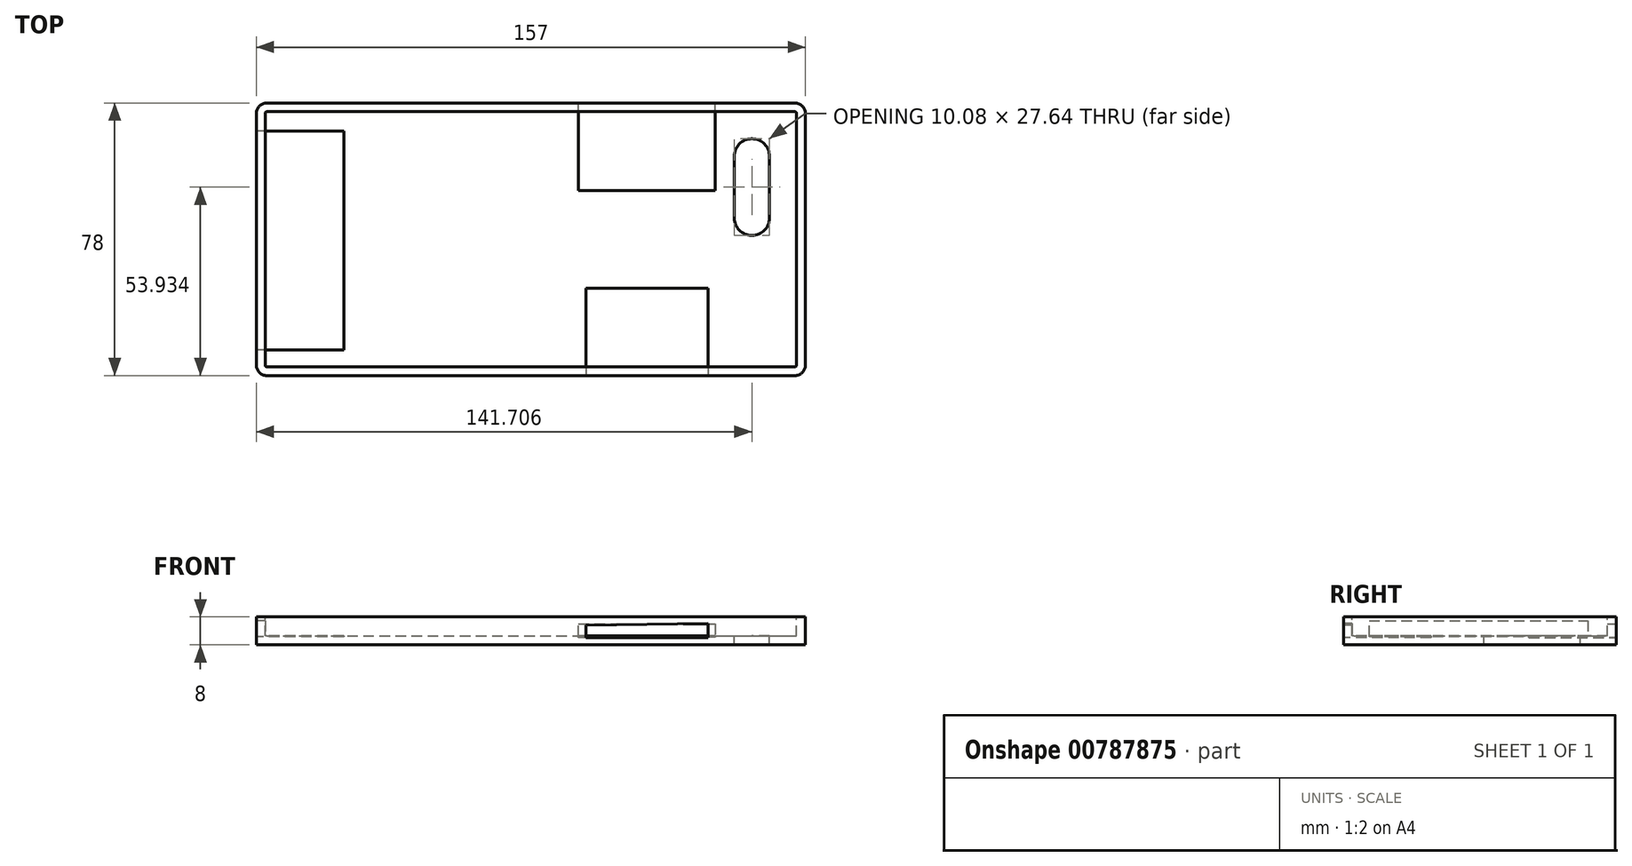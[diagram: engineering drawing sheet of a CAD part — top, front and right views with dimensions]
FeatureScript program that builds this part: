
annotation { "Feature Type Name" : "Feature", "Feature Type Description" : "" }
export const myFeature = defineFeature(function(context is Context, id is Id, definition is map)
    precondition{}
    {
        {
            var Q0;
            Q0=qCreatedBy(makeId("Top.planeOp"),FACE);
            var sketch = newSketch(context, id + "F0", { "sketchPlane" : qUnion([Q0])});
            skLineSegment(sketch, "E0.bottom", {"start": v(0, 0) * mm, "end": v(157, 0) * mm});
            skLineSegment(sketch, "E0.top", {"start": v(0, 78) * mm, "end": v(157, 78) * mm});
            skLineSegment(sketch, "E0.left", {"start": v(0, 0) * mm, "end": v(0, 78) * mm});
            skLineSegment(sketch, "E0.right", {"start": v(157, 0) * mm, "end": v(157, 78) * mm});
            skSolve(sketch);
        }
        {
            var Q0;
            Q0=makeQuery(id+"F0.imprint","IMPRINT",FACE,{"disambiguationData":[TD([[makeQuery(id+"F0.imprint","IMPRINT",EDGE,{"derivedFrom":sQuery(id+"F0.wireOp",EDGE,"E0.bottom")}),1.0]])]});
            extrude(context, id + "F1", {"entities" : qUnion([Q0]), "depth" : 8 * mm, "offsetDistance" : 25 * mm});
        }
        {
            var Q0;
            Q0=makeQuery(id+"F1.opExtrude","SWEPT_EDGE",EDGE,{"disambiguationData":[OSD([sQuery(id+"F0.wireOp",EDGE,"E0.bottom"),sQuery(id+"F0.wireOp",EDGE,"E0.right")])]});
            var Q1;
            Q1=makeQuery(id+"F1.opExtrude","SWEPT_EDGE",EDGE,{"disambiguationData":[OSD([sQuery(id+"F0.wireOp",EDGE,"E0.top"),sQuery(id+"F0.wireOp",EDGE,"E0.right")])]});
            var Q2;
            Q2=makeQuery(id+"F1.opExtrude","SWEPT_EDGE",EDGE,{"disambiguationData":[OSD([sQuery(id+"F0.wireOp",EDGE,"E0.top"),sQuery(id+"F0.wireOp",EDGE,"E0.left")])]});
            var Q3;
            Q3=makeQuery(id+"F1.opExtrude","SWEPT_EDGE",EDGE,{"disambiguationData":[OSD([sQuery(id+"F0.wireOp",EDGE,"E0.bottom"),sQuery(id+"F0.wireOp",EDGE,"E0.left")])]});
            fillet(context, id + "F2", {"entities" : qUnion([Q0, Q1, Q2, Q3]), "radius" : 3 * mm, "tangentPropagation" : true, "allowEdgeOverflow" : false});
        }
        {
            var Q0;
            Q0=makeQuery(id+"F1.opExtrude","CAP_FACE",FACE,{"disambiguationData":[OSD([sQuery(id+"F0.wireOp",EDGE,"E0.bottom"),sQuery(id+"F0.wireOp",EDGE,"E0.top"),sQuery(id+"F0.wireOp",EDGE,"E0.left"),sQuery(id+"F0.wireOp",EDGE,"E0.right")])],"isStart":false});
            shell(context, id + "F3", {"entities" : qUnion([Q0]), "thickness" : 2.5 * mm});
        }
        {
            var Q0;
            Q0=makeQuery(id+"F3.opShell","OFFSET_FACE",FACE,{"disambiguationData":[OSD([sQuery(id+"F0.wireOp",EDGE,"E0.bottom"),sQuery(id+"F0.wireOp",EDGE,"E0.top"),sQuery(id+"F0.wireOp",EDGE,"E0.left"),sQuery(id+"F0.wireOp",EDGE,"E0.right")])]});
            var sketch = newSketch(context, id + "F4", { "sketchPlane" : qUnion([Q0])});
            skLineSegment(sketch, "E1.bottom", {"start": v(141.74, 67.75) * mm, "end": v(141.67, 67.75) * mm});
            skLineSegment(sketch, "E1.top", {"start": v(141.74, 40.12) * mm, "end": v(141.67, 40.12) * mm});
            skLineSegment(sketch, "E1.left", {"start": v(146.74, 62.75) * mm, "end": v(146.74, 45.12) * mm});
            skLineSegment(sketch, "E1.right", {"start": v(136.67, 62.75) * mm, "end": v(136.67, 45.12) * mm});
            skPoint(sketch, "E2.visualSharp", {"position": v(146.74, 67.75) * mm});
            skArc(sketch, "E2.filletArc", {"start": v(146.74, 62.75) * mm, "mid": v(145.28, 66.29) * mm, "end": v(141.74, 67.75) * mm});
            skPoint(sketch, "E3.visualSharp", {"position": v(136.67, 67.75) * mm});
            skArc(sketch, "E3.filletArc", {"start": v(141.67, 67.75) * mm, "mid": v(138.13, 66.29) * mm, "end": v(136.67, 62.75) * mm});
            skPoint(sketch, "E4.visualSharp", {"position": v(136.67, 40.12) * mm});
            skArc(sketch, "E4.filletArc", {"start": v(136.67, 45.12) * mm, "mid": v(138.13, 41.58) * mm, "end": v(141.67, 40.12) * mm});
            skPoint(sketch, "E5.visualSharp", {"position": v(146.74, 40.12) * mm});
            skArc(sketch, "E5.filletArc", {"start": v(141.74, 40.12) * mm, "mid": v(145.28, 41.58) * mm, "end": v(146.74, 45.12) * mm});
            skSolve(sketch);
        }
        {
            var Q0;
            Q0=makeQuery(id+"F4.imprint","IMPRINT",FACE,{"disambiguationData":[TD([[makeQuery(id+"F4.imprint","IMPRINT",EDGE,{"derivedFrom":sQuery(id+"F4.wireOp",EDGE,"E1.bottom")}),1.0]])]});
            extrude(context, id + "F5", {"entities" : qUnion([Q0]), "operationType" : NewBodyOperationType.REMOVE, "oppositeDirection" : true, "depth" : 25 * mm, "offsetDistance" : 25 * mm});
        }
        {
            var Q0;
            Q0=makeQuery(id+"F1.opExtrude","SWEPT_FACE",FACE,{"disambiguationData":[OSD([sQuery(id+"F0.wireOp",EDGE,"E0.left")])]});
            var sketch = newSketch(context, id + "F6", { "sketchPlane" : qUnion([Q0])});
            skSolve(sketch);
        }
        {
            var Q0;
            {var subQ0=sQuery(id+"F0.wireOp",EDGE,"E0.left");Q0=makeQuery(id+"F6.imprint","IMPRINT",FACE,{"disambiguationData":[TD([[makeQuery(id+"F6.imprint","IMPRINT",EDGE,{"derivedFrom":makeQuery(id+"F1.opExtrude","CAP_EDGE",EDGE,{"disambiguationData":[OSD([subQ0])],"isStart":true})}),-1.0]])]});}
            var sketch = newSketch(context, id + "F7", { "sketchPlane" : qUnion([Q0])});
            skLineSegment(sketch, "E6", {"start": v(-69.9, 6.86) * mm, "end": v(-69.9, 2.36) * mm});
            skLineSegment(sketch, "E7", {"start": v(-69.9, 2.36) * mm, "end": v(-7.36, 2.36) * mm});
            skLineSegment(sketch, "E8", {"start": v(-7.36, 2.36) * mm, "end": v(-7.36, 6.86) * mm});
            skLineSegment(sketch, "E9", {"start": v(-7.36, 6.86) * mm, "end": v(-69.9, 6.86) * mm});
            skSolve(sketch);
        }
        {
            var Q0;
            Q0 = qSketchRegion(id + "F7", true);
            extrude(context, id + "F8", {"entities" : qUnion([Q0]), "operationType" : NewBodyOperationType.REMOVE, "oppositeDirection" : true, "depth" : 25 * mm, "offsetDistance" : 25 * mm});
        }
        {
            var Q0;
            Q0=makeQuery(id+"F1.opExtrude","SWEPT_FACE",FACE,{"disambiguationData":[OSD([sQuery(id+"F0.wireOp",EDGE,"E0.top")])]});
            var sketch = newSketch(context, id + "F9", { "sketchPlane" : qUnion([Q0])});
            skLineSegment(sketch, "E10", {"start": v(-92.13, 2) * mm, "end": v(-92.13, 5.97) * mm});
            skLineSegment(sketch, "E11", {"start": v(-92.13, 5.97) * mm, "end": v(-131.2, 5.97) * mm});
            skLineSegment(sketch, "E12", {"start": v(-131.2, 5.97) * mm, "end": v(-131.2, 2.24) * mm});
            skLineSegment(sketch, "E13", {"start": v(-131.2, 2.24) * mm, "end": v(-92.13, 2) * mm});
            skSolve(sketch);
        }
        {
            var Q0;
            Q0=makeQuery(id+"F1.opExtrude","SWEPT_FACE",FACE,{"disambiguationData":[OSD([sQuery(id+"F0.wireOp",EDGE,"E0.bottom")])]});
            var sketch = newSketch(context, id + "F10", { "sketchPlane" : qUnion([Q0])});
            skLineSegment(sketch, "E14", {"start": v(94.26, 5.59) * mm, "end": v(94.26, 2) * mm});
            skLineSegment(sketch, "E15", {"start": v(94.26, 2) * mm, "end": v(129.17, 2) * mm});
            skLineSegment(sketch, "E16", {"start": v(129.17, 2) * mm, "end": v(129.17, 6.07) * mm});
            skLineSegment(sketch, "E17", {"start": v(129.17, 6.07) * mm, "end": v(94.26, 5.59) * mm});
            skSolve(sketch);
        }
        {
            var Q0;
            Q0 = qSketchRegion(id + "F10", true);
            extrude(context, id + "F11", {"entities" : qUnion([Q0]), "operationType" : NewBodyOperationType.REMOVE, "oppositeDirection" : true, "depth" : 25 * mm, "offsetDistance" : 25 * mm});
        }
        {
            var Q0;
            Q0=makeQuery(id+"F9.imprint","IMPRINT",FACE,{"disambiguationData":[TD([[makeQuery(id+"F9.imprint","IMPRINT",EDGE,{"derivedFrom":sQuery(id+"F9.wireOp",EDGE,"E10")}),1.0]])]});
            extrude(context, id + "F12", {"entities" : qUnion([Q0]), "operationType" : NewBodyOperationType.REMOVE, "oppositeDirection" : true, "depth" : 25 * mm, "offsetDistance" : 25 * mm});
        }
    });
